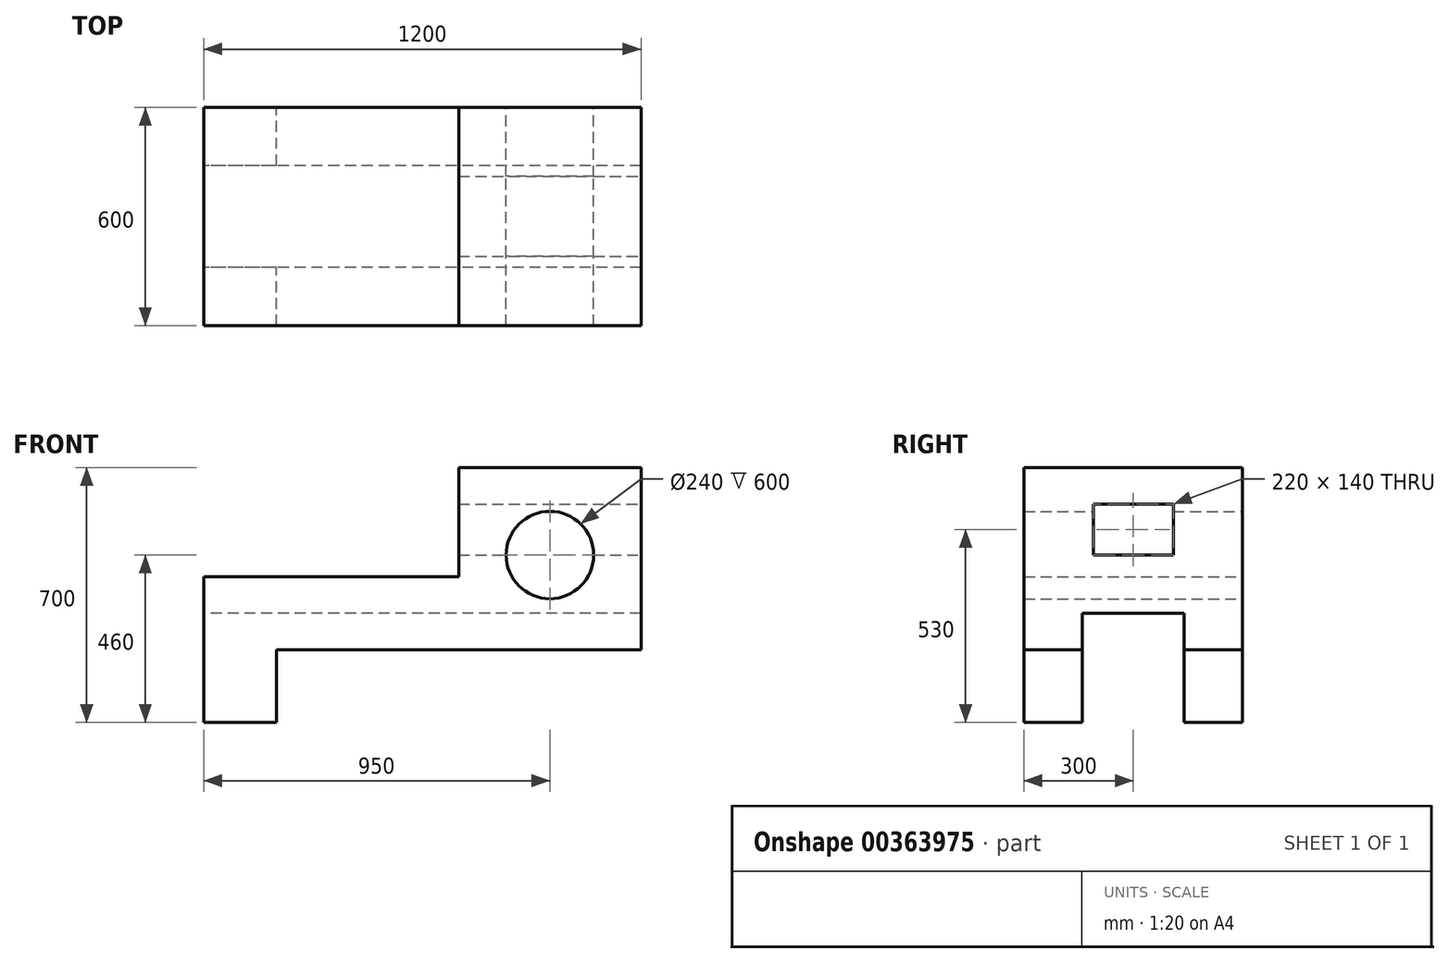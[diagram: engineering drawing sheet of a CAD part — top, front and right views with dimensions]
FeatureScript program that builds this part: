
annotation { "Feature Type Name" : "Feature", "Feature Type Description" : "" }
export const myFeature = defineFeature(function(context is Context, id is Id, definition is map)
    precondition{}
    {
        {
            var Q0;
            Q0=qCreatedBy(makeId("Front.planeOp"),FACE);
            var sketch = newSketch(context, id + "F0", { "sketchPlane" : qUnion([Q0])});
            skLineSegment(sketch, "E0.bottom", {"start": v(600, 350) * mm, "end": v(100, 350) * mm});
            skLineSegment(sketch, "E0.top", {"start": v(-400, -350) * mm, "end": v(-600, -350) * mm});
            skLineSegment(sketch, "E0.left", {"start": v(600, 350) * mm, "end": v(600, 50) * mm});
            skLineSegment(sketch, "E0.right", {"start": v(-600, 50) * mm, "end": v(-600, -350) * mm});
            skPoint(sketch, "E0.middle", {"position": v(0, 0) * mm});
            skLineSegment(sketch, "E1", {"start": v(600, 50) * mm, "end": v(600, -150) * mm});
            skLineSegment(sketch, "E2", {"start": v(-400, -350) * mm, "end": v(-400, -150) * mm});
            skLineSegment(sketch, "E3", {"start": v(-400, -150) * mm, "end": v(600, -150) * mm});
            skPoint(sketch, "E4.orphan", {"position": v(-400, 50) * mm});
            skLineSegment(sketch, "E5", {"start": v(-600, 50) * mm, "end": v(100, 50) * mm});
            skLineSegment(sketch, "E6", {"start": v(100, 50) * mm, "end": v(100, 350) * mm});
            skPoint(sketch, "E7.orphan", {"position": v(-600, 350) * mm});
            skPoint(sketch, "E8.orphan", {"position": v(600, -350) * mm});
            skPoint(sketch, "E9.end.orphan", {"position": v(350, 0) * mm});
            skPoint(sketch, "E10.end.orphan", {"position": v(350, 350) * mm});
            skLineSegment(sketch, "E11", {"start": v(600, -150) * mm, "end": v(600, 110) * mm});
            skLineSegment(sketch, "E12", {"start": v(600, 110) * mm, "end": v(350, 110) * mm});
            skCircle(sketch, "E13", {"center": v(350, 110) * mm, "radius": 120 * mm});
            skSolve(sketch);
        }
        {
            var Q0;
            Q0 = qSketchRegion(id + "F0", true);
            extrude(context, id + "F1", {"entities" : qUnion([Q0]), "depth" : 600 * mm});
        }
        {
            var Q0;
            Q0=makeQuery(id+"F1.opExtrude","SWEPT_FACE",FACE,{"disambiguationData":[OSD([sQuery(id+"F0.wireOp",EDGE,"E0.left"),sQuery(id+"F0.wireOp",EDGE,"E11")])]});
            var sketch = newSketch(context, id + "F2", { "sketchPlane" : qUnion([Q0])});
            skPoint(sketch, "E14.middle", {"position": v(-389.46, 180) * mm});
            skLineSegment(sketch, "E15", {"start": v(-600, 350) * mm, "end": v(-410, 350) * mm});
            skLineSegment(sketch, "E16", {"start": v(-410, 350) * mm, "end": v(-410, 250) * mm});
            skPoint(sketch, "E14.right.start.orphan", {"position": v(-559.06, 250) * mm});
            skPoint(sketch, "E14.top.end.orphan", {"position": v(-559.06, 110) * mm});
            skPoint(sketch, "E14.left.end.orphan", {"position": v(-219.86, 110) * mm});
            skPoint(sketch, "E14.left.start.orphan", {"position": v(-219.86, 250) * mm});
            skLineSegment(sketch, "E17.bottom", {"start": v(-410, 250) * mm, "end": v(-190, 250) * mm});
            skLineSegment(sketch, "E17.top", {"start": v(-410, 110) * mm, "end": v(-190, 110) * mm});
            skLineSegment(sketch, "E17.left", {"start": v(-410, 250) * mm, "end": v(-410, 110) * mm});
            skLineSegment(sketch, "E17.right", {"start": v(-190, 250) * mm, "end": v(-190, 110) * mm});
            skSolve(sketch);
        }
        {
            var Q0;
            Q0 = qSketchRegion(id + "F2", true);
            extrude(context, id + "F3", {"entities" : qUnion([Q0]), "operationType" : NewBodyOperationType.REMOVE, "endBound" : BoundingType.THROUGH_ALL, "oppositeDirection" : true, "depth" : 25.4 * mm});
        }
        {
            var Q0;
            Q0=makeQuery(id+"F1.opExtrude","SWEPT_FACE",FACE,{"disambiguationData":[OSD([sQuery(id+"F0.wireOp",EDGE,"E0.right")])]});
            var sketch = newSketch(context, id + "F4", { "sketchPlane" : qUnion([Q0])});
            skLineSegment(sketch, "E18.top", {"start": v(160, -50) * mm, "end": v(440, -50) * mm});
            skPoint(sketch, "E18.middle", {"position": v(300, -350) * mm});
            skPoint(sketch, "E19.start.orphan", {"position": v(160, -350) * mm});
            skPoint(sketch, "E20.end.orphan", {"position": v(440, -350) * mm});
            skPoint(sketch, "E21.orphan", {"position": v(440, -650) * mm});
            skPoint(sketch, "E22.orphan", {"position": v(160, -650) * mm});
            skLineSegment(sketch, "E23", {"start": v(160, -50) * mm, "end": v(160, -350) * mm});
            skLineSegment(sketch, "E24", {"start": v(440, -50) * mm, "end": v(440, -350) * mm});
            skSolve(sketch);
        }
        {
            var Q0;
            Q0 = qSketchRegion(id + "F4", true);
            var Q1;
            Q1=makeQuery(id+"F4.imprint","IMPRINT",FACE,{"disambiguationData":[TD([[makeQuery(id+"F4.imprint","IMPRINT",EDGE,{"derivedFrom":sQuery(id+"F4.wireOp",EDGE,"E18.top")}),-1.0]])]});
            extrude(context, id + "F5", {"entities" : qUnion([Q0, Q1]), "operationType" : NewBodyOperationType.REMOVE, "endBound" : BoundingType.THROUGH_ALL, "oppositeDirection" : true, "depth" : 25.4 * mm});
        }
    });
